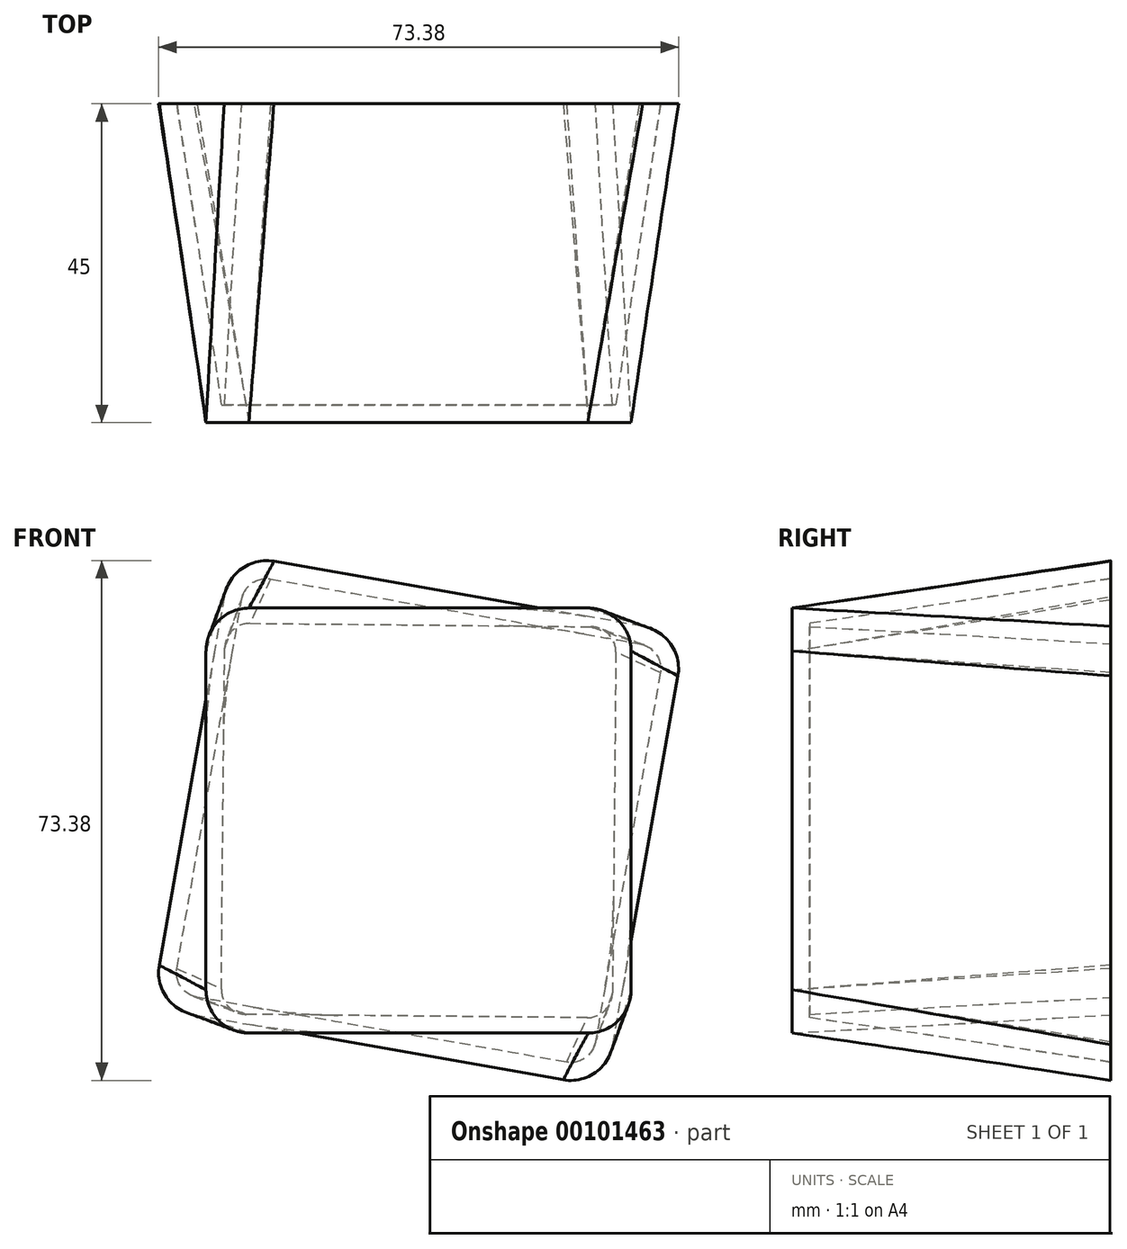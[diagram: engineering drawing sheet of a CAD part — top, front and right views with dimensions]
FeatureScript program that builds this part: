
annotation { "Feature Type Name" : "Feature", "Feature Type Description" : "" }
export const myFeature = defineFeature(function(context is Context, id is Id, definition is map)
    precondition{}
    {
        {
            var Q0;
            Q0=qCreatedBy(makeId("Front.planeOp"),FACE);
            var sketch = newSketch(context, id + "F0", { "sketchPlane" : qUnion([Q0])});
            skLineSegment(sketch, "E0.bottom", {"start": v(-30, 30) * mm, "end": v(30, 30) * mm});
            skLineSegment(sketch, "E0.top", {"start": v(-30, -30) * mm, "end": v(30, -30) * mm});
            skLineSegment(sketch, "E0.left", {"start": v(-30, 30) * mm, "end": v(-30, -30) * mm});
            skLineSegment(sketch, "E0.right", {"start": v(30, 30) * mm, "end": v(30, -30) * mm});
            skPoint(sketch, "E0.middle", {"position": v(0, 0) * mm});
            skSolve(sketch);
        }
        {
            var Q0;
            Q0=qCreatedBy(makeId("Front.planeOp"),FACE);
            cPlane(context, id + "F1", {"entities" : qUnion([Q0]), "cplaneType" : CPlaneType.OFFSET, "offset" : 45 * mm, "oppositeDirection" : true, "width" : 150 * mm, "height" : 150 * mm});
        }
        {
            var Q0;
            Q0=qCreatedBy(id+"F1.planeOp",FACE);
            var sketch = newSketch(context, id + "F2", { "sketchPlane" : qUnion([Q0])});
            skLineSegment(sketch, "E1", {"start": v(-26.36, 37.65) * mm, "end": v(-37.65, -26.36) * mm});
            skLineSegment(sketch, "E2", {"start": v(-37.65, -26.36) * mm, "end": v(26.36, -37.65) * mm});
            skLineSegment(sketch, "E3", {"start": v(26.36, -37.65) * mm, "end": v(37.65, 26.36) * mm});
            skLineSegment(sketch, "E4", {"start": v(37.65, 26.36) * mm, "end": v(-26.36, 37.65) * mm});
            skLineSegment(sketch, "E5", {"start": v(-26.36, 37.65) * mm, "end": v(26.36, -37.65) * mm});
            skLineSegment(sketch, "E6", {"start": v(-37.65, -26.36) * mm, "end": v(37.65, 26.36) * mm});
            skSolve(sketch);
        }
        {
            var Q0;
            Q0=qSketchRegion(id+"F0",true);
            var Q1;
            Q1=qSketchRegion(id+"F2",true);
            loft(context, id + "F3", {"sheetProfilesArray" : [{ "sheetProfileEntities" : qUnion([Q0]) }, { "sheetProfileEntities" : qUnion([Q1]) }]});
        }
        {
            var Q0;
            Q0=makeQuery(id+"F3.opLoft","SWEPT_EDGE",EDGE,{"disambiguationData":[OSD([sQuery(id+"F0.wireOp",EDGE,"E0.bottom"),sQuery(id+"F0.wireOp",EDGE,"E0.left"),sQuery(id+"F2.wireOp",EDGE,"E1"),sQuery(id+"F2.wireOp",EDGE,"E4"),sQuery(id+"F2.wireOp",EDGE,"E5")])]});
            var Q1;
            Q1=makeQuery(id+"F3.opLoft","SWEPT_EDGE",EDGE,{"disambiguationData":[OSD([sQuery(id+"F0.wireOp",EDGE,"E0.bottom"),sQuery(id+"F0.wireOp",EDGE,"E0.right"),sQuery(id+"F2.wireOp",EDGE,"E3"),sQuery(id+"F2.wireOp",EDGE,"E4"),sQuery(id+"F2.wireOp",EDGE,"E6")])]});
            var Q2;
            Q2=makeQuery(id+"F3.opLoft","SWEPT_EDGE",EDGE,{"disambiguationData":[OSD([sQuery(id+"F0.wireOp",EDGE,"E0.top"),sQuery(id+"F0.wireOp",EDGE,"E0.right"),sQuery(id+"F2.wireOp",EDGE,"E2"),sQuery(id+"F2.wireOp",EDGE,"E3"),sQuery(id+"F2.wireOp",EDGE,"E5")])]});
            var Q3;
            Q3=makeQuery(id+"F3.opLoft","SWEPT_EDGE",EDGE,{"disambiguationData":[OSD([sQuery(id+"F0.wireOp",EDGE,"E0.top"),sQuery(id+"F0.wireOp",EDGE,"E0.left"),sQuery(id+"F2.wireOp",EDGE,"E1"),sQuery(id+"F2.wireOp",EDGE,"E2"),sQuery(id+"F2.wireOp",EDGE,"E6")])]});
            fillet(context, id + "F4", {"entities" : qUnion([Q0, Q1, Q2, Q3]), "radius" : 6 * mm, "tangentPropagation" : true, "allowEdgeOverflow" : false});
        }
        {
            var Q0;
            {var subQ0=sQuery(id+"F2.wireOp",EDGE,"E4");Q0=makeQuery(id+"F3.opLoft","CAP_FACE",FACE,{"disambiguationData":[OSD([makeQuery(id+"F2.imprint","IMPRINT",FACE,{"disambiguationData":[TD([[makeQuery(id+"F2.imprint","IMPRINT",EDGE,{"derivedFrom":subQ0}),1.0]])]})])],"isStart":true});}
            shell(context, id + "F5", {"entities" : qUnion([Q0]), "thickness" : 2.5 * mm});
        }
    });
